# Revit family: IS_iLifeA_T4514_BIM_NL
name_source: partatom
category: Plumbing Fixtures
units: mm (PartAtom-declared; Revit-internal decimal feet)

## family parameters
Always vertical = No
Cut with Voids When Loaded = No
OmniClass Number = 23.45.05.14.14
OmniClass Title = Sinks/Lavatories
Part Type = Normal
Room Calculation Point = No
Round Connector Dimension = Use Diameter
Shared = No
Work Plane-Based = No

## types (2) — shared parameters
Accessories = https://www.idealstandard.nl
Afmetingen = 360 x 180 x 400mm
AfstandsEenheid = Millimeter
AreaMeasurement = internal
AreaUnits = Millimeter
Artikelreferentie = I.life A handrinse 40 cm with center taphole with overflow
Auteur = Ideal Standard
BIMObjectName = IS_IdealStandard_Wallhunghandrinsebasins_I.life_T4514
BIMobject category = Sanitary Basins
BIMobject category code = sanitary-basins
BIMobject main category = Sanitary
BIMobject main category code = sanitary
Beschrijvinggarantie = Herstellergarantie
Bestanddelen = Handwaschbecken 40 cm mit mittlerem Hahnloch mit Überlauf
BimObjectNaam = IS_IdealStandard_Wallhunghandrinsebasins_I.life_T4514
Brand url = https://www.idealstandard.nl
ConnectionType = Plumbing
CurrencyUnit = €
CurrentRevision = 1
Date of publishing = 28/06/2021
DurationUnit = Years
DuurEenheid = Jaar
Edition number = 1
Eigenschappen = Handwaschbecken 40 cm mit mittlerem Hahnloch mit Überlauf
Features = Handwaschbecken 40 cm mit mittlerem Hahnloch mit Überlauf
Garantieonderdelen = 5
Garantieunits = Jaar
Help = https://www.idealstandard.nl
Hoogte = 180.01514
Hulp = https://www.idealstandard.nl
IFC Classification = Sanitary Terminal
IfcExportAs = IfcSanitaryTerminalType
IfcExportType = WASHHANDBASIN
Installatieinstructies = https://www.idealstandard.nl
Installation instructions = https://www.idealstandard.nl
InstallationInstructions = https://www.idealstandard.nl
Lengte = 360 mm
LinearUnits = millimeter
MaintenanceInformation = https://www.idealstandard.nl
Manufacturer = Ideal Standard
Manufacturer name = Ideal Standard
ManufacturerURL = https://www.idealstandard.nl
Masterformat 2014 Code = 33 47 26.16
Masterformat 2014 Description = Retention Basins
Material = Vitrous China
Material main = Vitrous China
Merk = Ideal Standard
ModelReference = I.life A handrinse 40 cm with center taphole with overflow
Montageinstuctie = Wandhangende wastafels
NBS Reference Code = 35-79-94
NBS Reference Description = Wall-Hung Wash Basins
Name = Wallhunghandrinsebasins_I.life_T4514_IdealStandard
NettWeight = 10.6
NominalDepth = 360 mm
NominalHeight = 180 mm
NominalWidth = 400 mm
Normen = Wallhunghandrinsebasins_I.life_T4514_IdealStandard
OmniClass Code = 23-39 29 13 21 19
OmniClass Description = Surface Water Retention Basins
Ophangingwastafel = Wandhangende wastafels
OppervlakteEenheid = millimeter
Product Guid = 02e502aa-6a9c-4893-8356-cce95a7193bf
Product SKU = T4514
Product certification = https://www.idealstandard.nl
Product data url = https://bimobject.com
Product family = I.life
Product group = Handrinse Basin
Product name = I.life A handrinse 40 cm with center taphole with overflow
Product url = https://www.idealstandard.nl
ProductInformation = https://www.idealstandard.nl
ProductSoort = Wastafel
Productinformatie = https://www.idealstandard.nl
QR code = http://bimobject.com
Referentie = I.life A handrinse 40 cm with center taphole with overflow
Revisie = 1
Shape = sculpture
Size = 360 x 180 x 400mm
Space = Internal
SpareParts = https://www.idealstandard.nl
Technical description = https://www.idealstandard.nl
Telefoonnummer = 077 355 08 08
Typeconnectie = loodgieter
Typewastafel = wandhangende wastafel
URL = https://https:
Uniclass 1.4 Code = L7212
Uniclass 1.4 Description = Washbasins
Uniclass 2.0 Code = PR-35-79-94
Uniclass 2.0 Description = Wall-Hung Wash Basins
Uniclass 2015 Code = Pr_40_20_96_96
Uniclass 2015 Name = Wall-hung wash basins
Uniclass2015Beschrijving = Wall-hung hand rinse basins
Uniclass2015Code = Pr_40_20_96_95
Uniclass2015Referentie = Pr_40_20_96_95
Uniclass2015Title = Wall-hung hand rinse basins
Uniclass2015Version = v1.20
Urlproducent = https://https:
ValutaEenheid = €
Versie = 1
Version = 1
VolumeUnits = liters
Volumeunits = liters
Vorm = beeldhouwwerk
WRASURL = https://www.wrasapprovals.co.uk
WaarborgGarantieInstallatie = https://www.idealstandard.nl
WarrantyDescription = manufacturer warranty
WarrantyDurationParts = 99
WarrantyDurationUnit = years
Wisselstukken = https://www.idealstandard.nl
Youtube clip = https://www.youtube.com
zero-valued in all types: Breedte, BrutoGewicht, Cost, Diepte, DrainSize, GrootteAfvoergat, Nettogewicht, Overloop, Vervangingskosten

## per-type parameters (varying)
| type | Afwerking | Artikelnummer | Artikelomschrijving | BarCode | Color | Description | Finish | GTIN code | Kleur | MainColor | Model | ModelNumber | WashHandBasinMounting | WashHandBasinType |
| T4514MA - I.life A handrinse 40 cm with center taphole with overflow - Ideal Plus White | IdealPlusWeiß | T4514MA | I.life A handspoeling 40 cm met kraangat in het midden met overloop - Ideal Plus White | 8014140486718 | IdealPlusWeiß | I.life A handspoeling 40 cm met kraangat in het midden met overloop - Ideal Plus White | IdealPlusWeiß | https://8014140486718 | IdealPlusWeiß | IdealPlusWeiß | T4514MA | T4514MA | Wall Hung | Washbasin |
| T451401 - I.life A handrinse 40 cm with center taphole with overflow - White | Weiß | T451401 | I.life A handspoeling 40 cm met kraangat in het midden met overloop - Wit | 8014140485827 | Weiß | I.life A handspoeling 40 cm met kraangat in het midden met overloop - Wit | Weiß | https://8014140485827 | Weiß | Weiß | T451401 | T451401 |  |  |

## geometry (parser evidence)
native form markers: Sweep x2
no freeform markers — native parametric forms only
